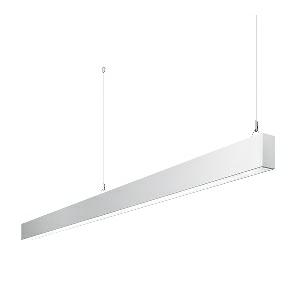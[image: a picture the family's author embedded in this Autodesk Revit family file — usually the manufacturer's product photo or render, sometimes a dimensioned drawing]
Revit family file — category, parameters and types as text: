
# Revit family: dotoo_line_-_dlp_3000_830_d_end_00805812_41ba
name_source: partatom
category: Lighting Fixtures
units: mm (PartAtom-declared; Revit-internal decimal feet)

## family parameters
Cut with Voids When Loaded = No
Host = Face
Light Source = No
Part Type = Normal
Room Calculation Point = No
Round Connector Dimension = Use Diameter
Shared = No

## types (1)
- DOTOO.line - DLP 3000/830/D END (1 x LED, 2650 lm, 3000K)
    Apparent Load = 26 VA
    Approval mark = CE
    CIE Flux Codes = 67 91 98 100 100
    Color Rendering = 80-89
    Color Temperature = 3000K
    Control Gear = Electronic ballast
    Default Elevation = 1800 mm
    Description = DLP 3000/830/D|Suspended luminaire|light source: LED|connected load: 220-240 V, 50/60 Hz|Power consumption: approx. 26 W|standby: approx. 0,15|luminous flux: 2650 lm|luminous efficacy: 101 lm/W|light distribution: Direct|direct ratio: approx. 100 %|colour temperature: Warm white, ca. 3000 K|color rendering index (CRI): >= 80|chromaticity tolerance:  3 SDCM|System of protection: IP 40|technology: Continuously dimmable|luminaire body|material: Sectional aluminium|colour: White|lamp cover: Acrylic (PMMA), Clear|mains lead: 1,0 m With free stranded wires|Fastening: Steel cable 0.3 - 0.7 m|glare control: Prism aperture|luminance(L65): <= 3000 cd/m|unified glare rating(4H 8H): <=  19|special features: DALI Load 1x, TouchDIM - dimming via standard switch, Through-wired, up to 18 m on one mains connection, Flicker-free, Suitable as emergency lighting, Mechanical and electrical connection of the individual modules without tools|
    Frequency = 50 Hz
    Height = 110 mm
    Lamp = 1 x LED
    Lamp Light Flux = 2650 lm
    Lamp count = 1
    Length = 2250 mm
    Luminous efficacy = 102 lm/W
    Manufacturer = Waldmann
    ModVariant = No
    Model = 00805812
    Mounting Place = Ceiling
    Mounting Type = Pendant
    Number of Poles = 1
    OnlyDefault = Yes
    Power Factor = 1
    Product Name = DOTOO.line - DLP 3000/830/D END
    Product group = Suspended luminaire
    ProductGroupID = 9
    Protection Class = Protection class I
    Protection Degree = IP 40
    RLX_Detail_Level = 1
    RLX_Emergency_Light_Flux = 0 lm
    RLX_Emergency_Type = 0
    RLX_Emergency_Type_DB = No
    RlxData = <blob elided: 21057 chars, md5=d9c4279d>
    Socket = socket
    Standby Power = 0 W
    System Light Flux = 2650 lm
    System Power = 26 W
    Type Comments = Product without accessories
    Type Image = 113315000-00692609.jpg
    URL = http://relux.com
    VarID = ---
    Voltage = 230 V
    Voltage Range = 220-240 V
    Weight = 0.00 kg
    Width = 60 mm  [stored 0.19685 ft]

note: [stored X ft] marks values corroborated as IEEE doubles in the binary element streams (Revit-internal decimal feet)

## geometry (parser evidence)
native form markers: Blend x4, Sweep x10
no freeform markers — native parametric forms only
